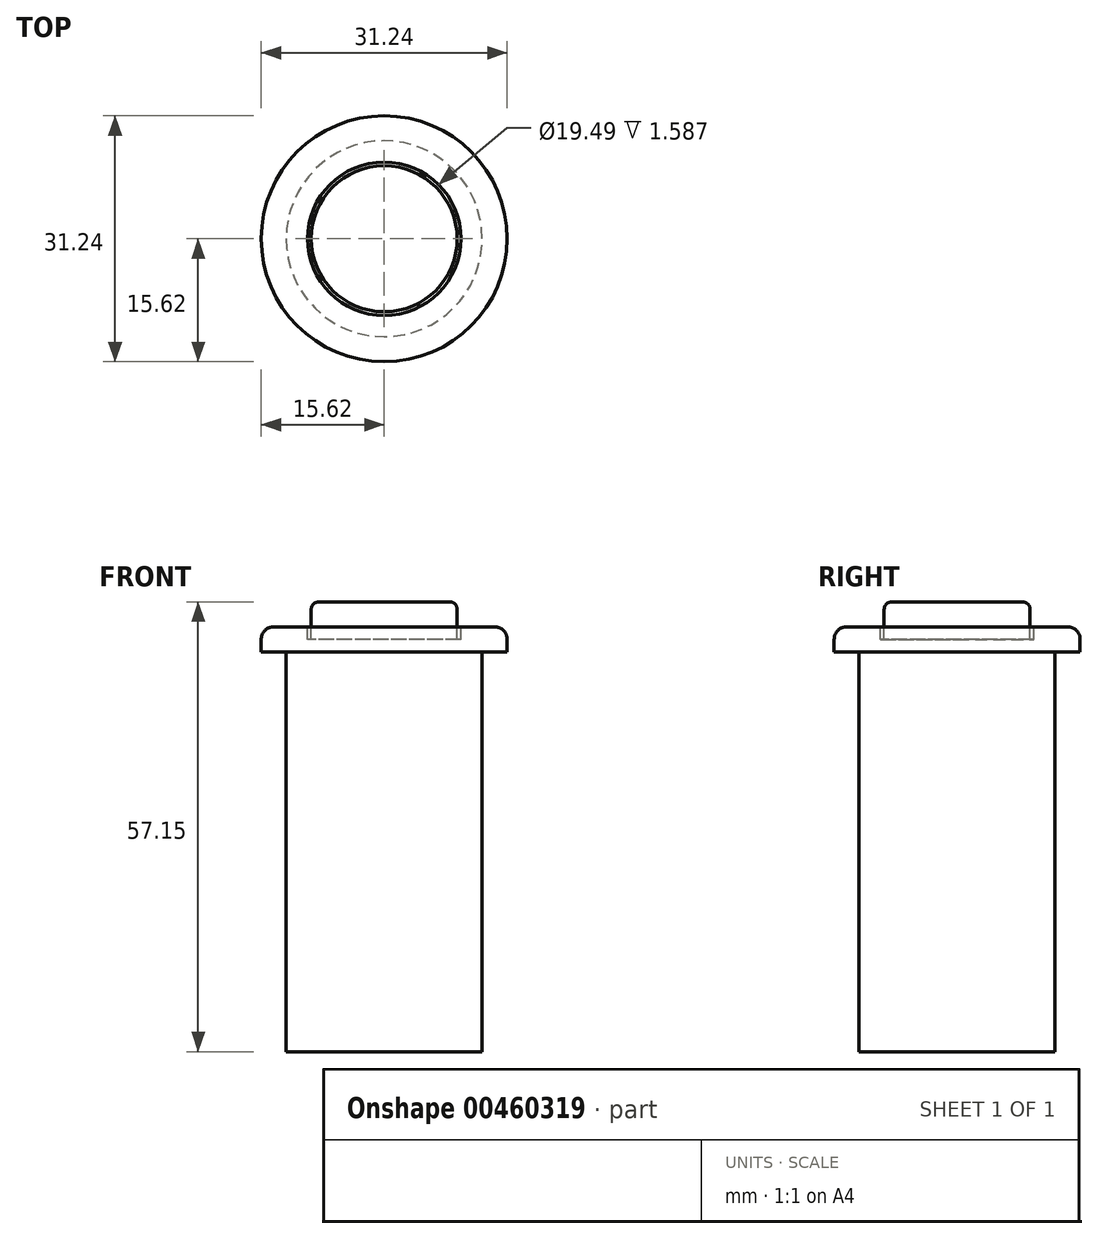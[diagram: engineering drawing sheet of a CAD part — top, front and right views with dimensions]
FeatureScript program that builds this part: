
annotation { "Feature Type Name" : "Feature", "Feature Type Description" : "" }
export const myFeature = defineFeature(function(context is Context, id is Id, definition is map)
    precondition{}
    {
        {
            var Q0;
            Q0=qCreatedBy(makeId("Front.planeOp"),FACE);
            var sketch = newSketch(context, id + "F0", { "sketchPlane" : qUnion([Q0])});
            skLineSegment(sketch, "E0", {"start": v(12.45, 25.4) * mm, "end": v(12.45, -25.4) * mm});
            skLineSegment(sketch, "E1", {"start": v(12.45, -25.4) * mm, "end": v(0, -25.4) * mm});
            skLineSegment(sketch, "E2", {"start": v(0, -25.4) * mm, "end": v(0, 31.75) * mm});
            skLineSegment(sketch, "E3", {"start": v(0, 31.75) * mm, "end": v(8.32, 31.75) * mm});
            skLineSegment(sketch, "E4", {"start": v(9.27, 30.8) * mm, "end": v(9.27, 28.58) * mm});
            skLineSegment(sketch, "E5", {"start": v(9.74, 28.57) * mm, "end": v(14.03, 28.57) * mm});
            skLineSegment(sketch, "E6", {"start": v(15.62, 26.99) * mm, "end": v(15.62, 25.4) * mm});
            skLineSegment(sketch, "E7", {"start": v(15.62, 25.4) * mm, "end": v(12.45, 25.4) * mm});
            skLineSegment(sketch, "E8", {"start": v(9.27, 28.57) * mm, "end": v(9.27, 26.99) * mm});
            skLineSegment(sketch, "E9", {"start": v(9.27, 26.99) * mm, "end": v(9.74, 26.99) * mm});
            skLineSegment(sketch, "E10", {"start": v(9.74, 26.99) * mm, "end": v(9.74, 28.58) * mm});
            skPoint(sketch, "E11.visualSharp", {"position": v(9.27, 31.75) * mm});
            skArc(sketch, "E11.filletArc", {"start": v(9.27, 30.8) * mm, "mid": v(9, 31.47) * mm, "end": v(8.32, 31.75) * mm});
            skPoint(sketch, "E12.visualSharp", {"position": v(15.62, 28.57) * mm});
            skArc(sketch, "E12.filletArc", {"start": v(15.62, 26.99) * mm, "mid": v(15.16, 28.11) * mm, "end": v(14.03, 28.58) * mm});
            skLineSegment(sketch, "E13", {"start": v(0, 48.54) * mm, "end": v(0, -52.9) * mm, "construction": true});
            skSolve(sketch);
        }
        {
            var Q0;
            Q0 = qSketchRegion(id + "F0", true);
            var Q1;
            Q1=sQuery(id+"F0.wireOp",EDGE,"E13");
            revolve(context, id + "F1", {"entities" : qUnion([Q0]), "axis" : qUnion([Q1]), "revolveType" : RevolveType.FULL});
        }
    });
